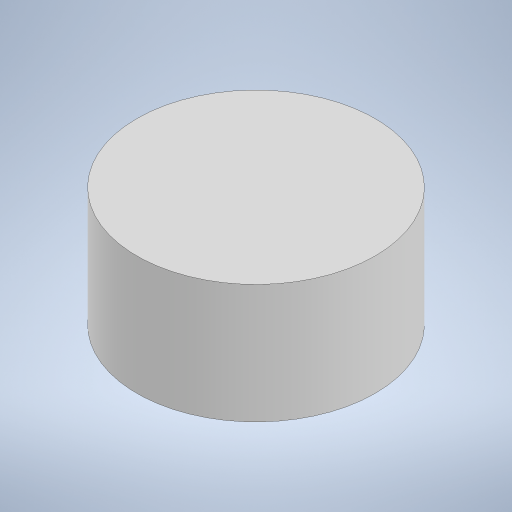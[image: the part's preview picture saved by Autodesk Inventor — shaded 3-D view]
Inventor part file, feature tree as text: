
AUTODESK INVENTOR PART (.ipt)
format: ipt  version: 2023 (Build 270158000, 158)  size: 186,368 bytes
history: native  units: mm
features: extrude x1, sketch x1
ambient origin geometry x8: Origin, YZ Plane, XZ Plane, XY Plane, X Axis, Y Axis, Z Axis, Center Point
bodies: Solid1 (feature_tree)
feature tree (2):
  extrude  "Extrusion1"  Depth=5.0mm TaperAngle=0.0deg
  sketch  "Sketch1"  dims[d0=10.0mm d1=5.0mm d2=0.0mm]
